# Revit family: PRD_FrankeWS_WshbsnSpts_F3Aerator_ASXX1008
name_source: partatom
category: Specialty Equipment
revit_build: Autodesk Revit 2018 (Build: 20190510_1515(x64)
units: mm (PartAtom-declared; Revit-internal decimal feet)

## family parameters
Always vertical = No
Cut with Voids When Loaded = No
OmniClass Number = 23.45.05.14.99
OmniClass Title = Other Sanitary Washing Plumbing Fixtures
Part Type = Normal
Room Calculation Point = No
Round Connector Dimension = Use Diameter
Shared = No
Work Plane-Based = Yes

## types (1)
- ASXX1008
    AssetType = Fixed
    BIMObjectName = PRD_AR_WashbasinSpouts_F3Aerator_ASXX1008
    BodyMaterial = PRD_AR_ChromatedBrass_HighPolished
    Category = Pr_40_20_87_97, Washbasin spouts
    Default Elevation = 1219 mm
    Description = Aerator M 24 x 1, with integrated flow rate regulator 3.0 l/min. Packing unit 10 pieces
    DurationUnit = year
    Features = integrated flow rate regulator 3.0 l/min
    GrossWeight = 0.13 kg
    IfcExportAs = IfcSanitaryTerminalType
    IfcExportType = USERDEFINED
    Manufacturer = KWC Group AG
    ManufacturerName = KWC Group AG
    ManufacturerURL = www.kwc.com
    Model = ASXX1008
    ModelNumber = 2030041424
    ModelReference = ASXX1008
    Name = F3 3.0 l/min. aerator ASXX1008
    NetWeight = 0.12 kg
    NominalDepth = 0 mm  [stored 0 ft]
    NominalHeight = 0 mm  [stored 0 ft]
    NominalLength = 0 mm  [stored 0 ft]
    NominalWidth = 0 mm  [stored 0 ft]
    ProductCode = 208.0599.665
    ProductInformation = https://pim.kwc.com
    Quantity = 10
    QuantityUom = Pieces
    Status = New
    TailorMade = No
    URL = www.kwc.com
    Uniclass2015Code = Pr_40_20_87_97
    Uniclass2015Title = Washbasin spouts
    Uniclass2015Version = Products v1.23
    Version = 1
    WarrantyDurationUnit = year

note: [stored X ft] marks values corroborated as IEEE doubles in the binary element streams (Revit-internal decimal feet)

## geometry (parser evidence)
native form markers: Sweep x3
no freeform markers — native parametric forms only
